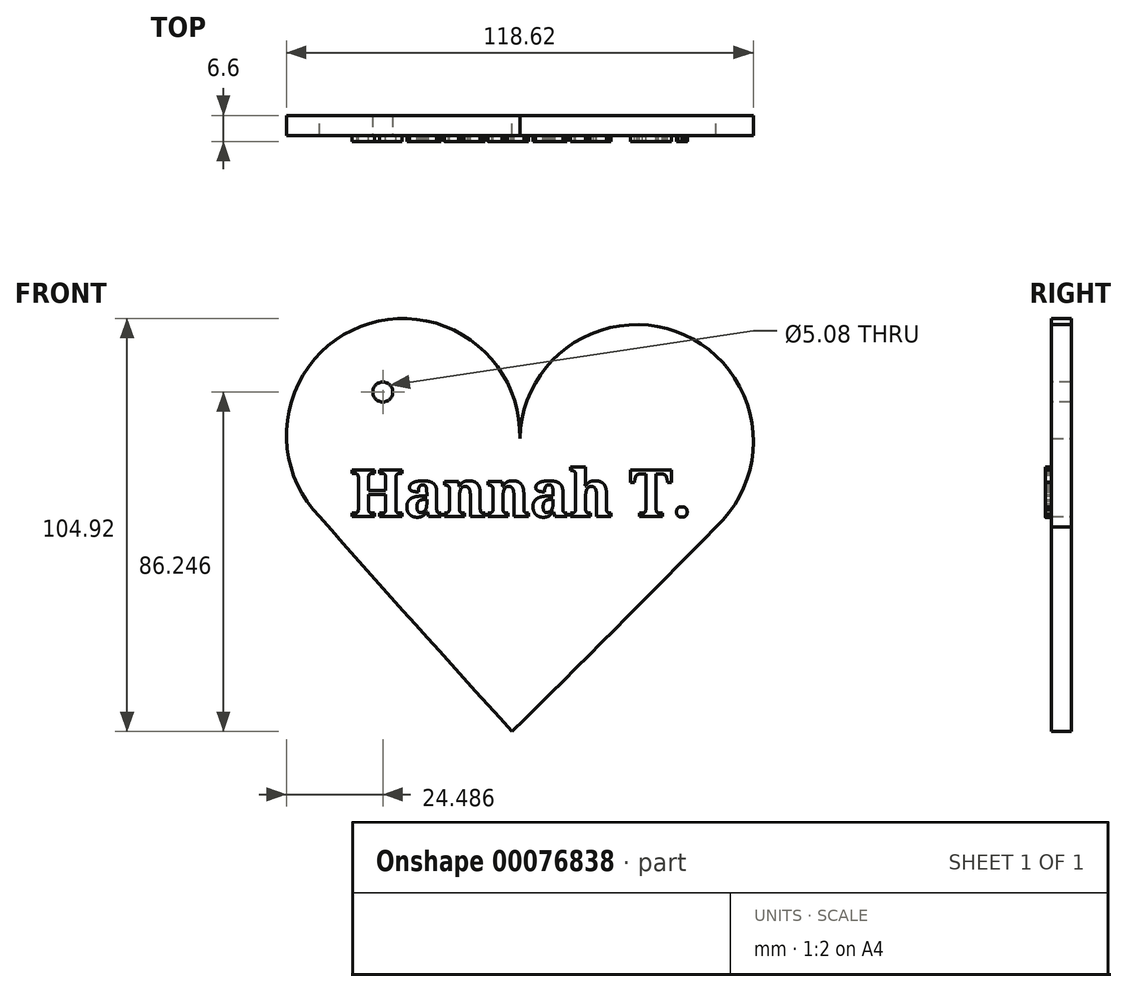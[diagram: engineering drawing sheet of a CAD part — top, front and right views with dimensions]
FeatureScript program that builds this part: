
annotation { "Feature Type Name" : "Feature", "Feature Type Description" : "" }
export const myFeature = defineFeature(function(context is Context, id is Id, definition is map)
    precondition{}
    {
        {
            var Q0;
            Q0=qCreatedBy(makeId("Front.planeOp"),FACE);
            var sketch = newSketch(context, id + "F0", { "sketchPlane" : qUnion([Q0])});
            skCircle(sketch, "E0", {"center": v(-36.52, 40.57) * mm, "radius": 29.66 * mm});
            skArc(sketch, "E1", {"start": v(-57.8, 19.9) * mm, "mid": v(-33.41, -7.5) * mm, "end": v(-8.8, -34.69) * mm});
            skLineSegment(sketch, "E2", {"start": v(-6.23, 64.45) * mm, "end": v(-8.98, -41.27) * mm, "construction": true});
            skCircle(sketch, "E3.MirrorC", {"center": v(22.78, 39.03) * mm, "radius": 29.66 * mm});
            skArc(sketch, "E4.MirrorCS", {"start": v(42.95, 17.28) * mm, "mid": v(17.18, -8.81) * mm, "end": v(-8.8, -34.69) * mm});
            skSolve(sketch);
        }
        {
            var Q0;
            Q0 = qSketchRegion(id + "F0", true);
            extrude(context, id + "F1", {"entities" : qUnion([Q0]), "depth" : 5.08 * mm});
        }
        {
            var Q0;
            Q0=makeQuery(id+"F1.opExtrude","CAP_FACE",FACE,{"disambiguationData":[OSD([sQuery(id+"F0.wireOp",EDGE,"E0"),sQuery(id+"F0.wireOp",EDGE,"E1"),sQuery(id+"F0.wireOp",EDGE,"E3.MirrorC"),sQuery(id+"F0.wireOp",EDGE,"E4.MirrorCS")])],"isStart":false});
            var sketch = newSketch(context, id + "F2", { "sketchPlane" : qUnion([Q0])});
            skText(sketch, "E5", { "text": "Hannah T.", "fontName": "NotoSerif-Bold.ttf"});
            const initialGuessF2  = {"E5": [-0.04992, 0.01989, 1, 0, 0.01194]};
            skSetInitialGuess(sketch, initialGuessF2);
            skSolve(sketch);
        }
        {
            var Q0;
            Q0 = qSketchRegion(id + "F2", true);
            extrude(context, id + "F3", {"entities" : qUnion([Q0]), "operationType" : NewBodyOperationType.ADD, "depth" : 1.52 * mm});
        }
        {
            var Q0;
            {var subQ0=sQuery(id+"F0.wireOp",EDGE,"E1");var subQ1=sQuery(id+"F0.wireOp",EDGE,"E4.MirrorCS");var subQ2=sQuery(id+"F0.wireOp",EDGE,"E0");var subQ3=sQuery(id+"F0.wireOp",EDGE,"E3.MirrorC");Q0=makeQuery(id+"F3.boolean.opBoolean","SPLIT",FACE,{"disambiguationData":[TD([makeQuery(id+"F1.opExtrude","SWEPT_FACE",FACE,{"disambiguationData":[OSD([subQ2])]})])],"derivedFrom":makeQuery(id+"F1.opExtrude","CAP_FACE",FACE,{"disambiguationData":[OSD([subQ2,subQ0,subQ3,subQ1])],"isStart":false})});}
            var sketch = newSketch(context, id + "F4", { "sketchPlane" : qUnion([Q0])});
            skLineSegment(sketch, "E6", {"start": v(-66.18, 40.03) * mm, "end": v(-17.21, 63.08) * mm, "construction": true});
            skCircle(sketch, "E7", {"center": v(-41.7, 51.56) * mm, "radius": 2.54 * mm});
            skSolve(sketch);
        }
        {
            var Q0;
            Q0 = qSketchRegion(id + "F4", true);
            extrude(context, id + "F5", {"entities" : qUnion([Q0]), "operationType" : NewBodyOperationType.REMOVE, "endBound" : BoundingType.THROUGH_ALL, "oppositeDirection" : true, "depth" : 25.4 * mm});
        }
    });
